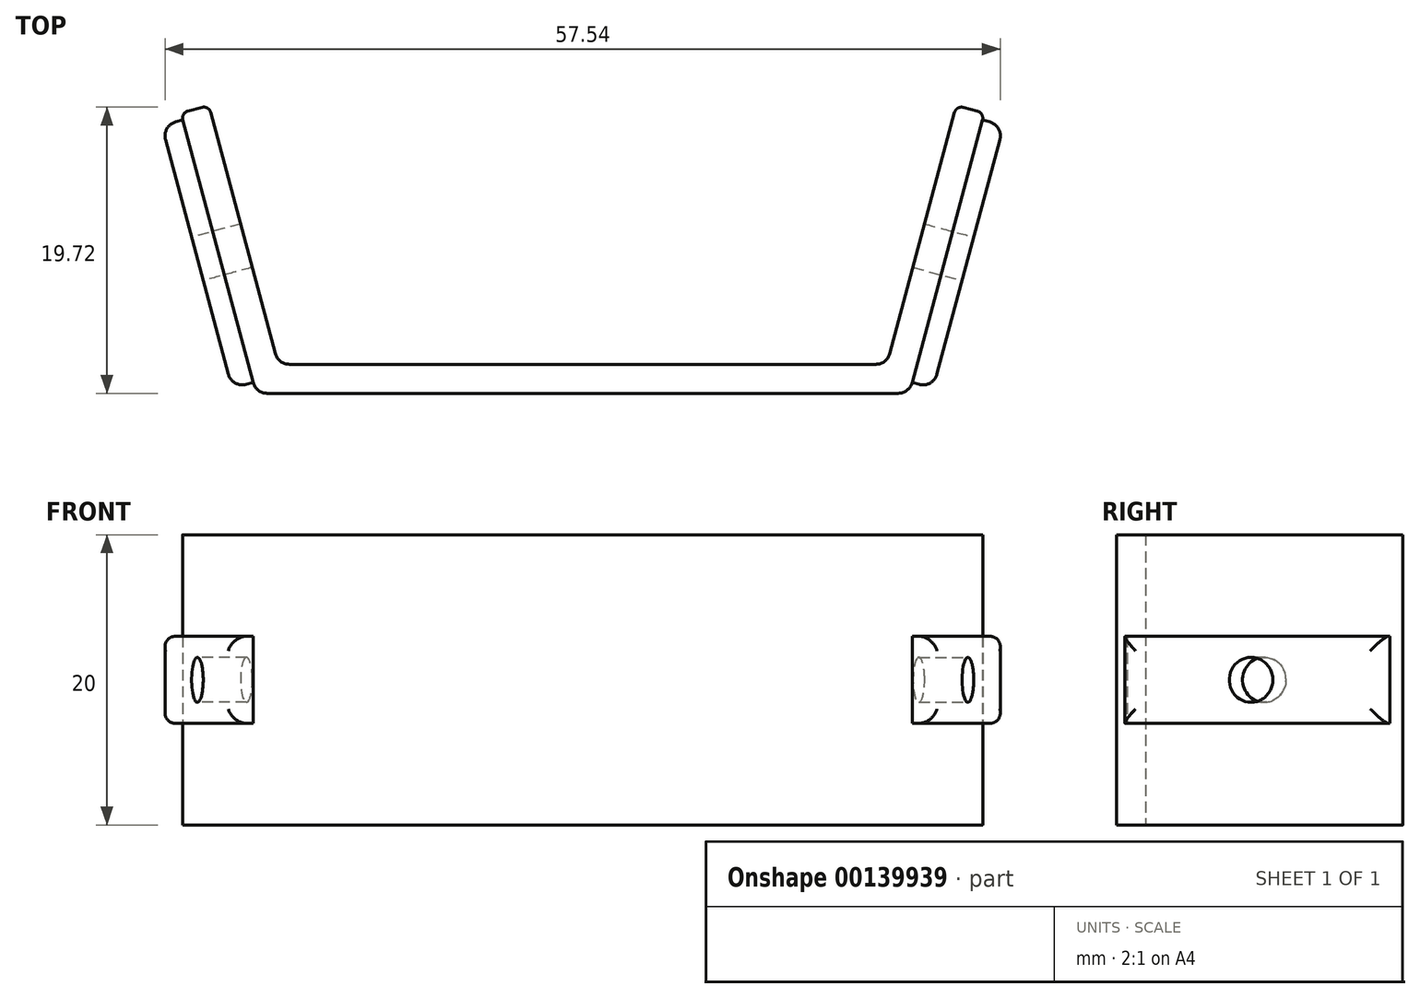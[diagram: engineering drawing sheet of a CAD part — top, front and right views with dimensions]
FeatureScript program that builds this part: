
annotation { "Feature Type Name" : "Feature", "Feature Type Description" : "" }
export const myFeature = defineFeature(function(context is Context, id is Id, definition is map)
    precondition{}
    {
        {
            var Q0;
            Q0=qCreatedBy(makeId("Top.planeOp"),FACE);
            var sketch = newSketch(context, id + "F0", { "sketchPlane" : qUnion([Q0])});
            skLineSegment(sketch, "E0", {"start": v(0.77, 0) * mm, "end": v(44.23, 0) * mm});
            skLineSegment(sketch, "E1", {"start": v(45.2, 0.74) * mm, "end": v(50.05, 18.84) * mm});
            skLineSegment(sketch, "E2", {"start": v(49.7, 19.45) * mm, "end": v(48.73, 19.7) * mm});
            skLineSegment(sketch, "E3", {"start": v(48.12, 19.35) * mm, "end": v(43.66, 2.74) * mm});
            skLineSegment(sketch, "E4", {"start": v(42.7, 2) * mm, "end": v(2.3, 2) * mm});
            skLineSegment(sketch, "E5", {"start": v(1.34, 2.74) * mm, "end": v(-3.12, 19.35) * mm});
            skLineSegment(sketch, "E6", {"start": v(-3.73, 19.7) * mm, "end": v(-4.7, 19.45) * mm});
            skLineSegment(sketch, "E7", {"start": v(-5.05, 18.84) * mm, "end": v(-0.2, 0.74) * mm});
            skPoint(sketch, "E8.visualSharp", {"position": v(-3.24, 19.84) * mm});
            skArc(sketch, "E8.filletArc", {"start": v(-3.12, 19.35) * mm, "mid": v(-3.35, 19.66) * mm, "end": v(-3.73, 19.7) * mm});
            skPoint(sketch, "E9.visualSharp", {"position": v(-5.18, 19.32) * mm});
            skArc(sketch, "E9.filletArc", {"start": v(-4.7, 19.45) * mm, "mid": v(-5, 19.21) * mm, "end": v(-5.05, 18.84) * mm});
            skPoint(sketch, "E10.visualSharp", {"position": v(0, 0) * mm});
            skArc(sketch, "E10.filletArc", {"start": v(-0.2, 0.74) * mm, "mid": v(0.16, 0.2) * mm, "end": v(0.77, 0) * mm});
            skPoint(sketch, "E11.visualSharp", {"position": v(1.53, 2) * mm});
            skArc(sketch, "E11.filletArc", {"start": v(1.34, 2.74) * mm, "mid": v(1.7, 2.2) * mm, "end": v(2.3, 2) * mm});
            skPoint(sketch, "E12.visualSharp", {"position": v(45, 0) * mm});
            skArc(sketch, "E12.filletArc", {"start": v(44.23, 0) * mm, "mid": v(44.84, 0.2) * mm, "end": v(45.2, 0.74) * mm});
            skPoint(sketch, "E13.visualSharp", {"position": v(43.47, 2) * mm});
            skArc(sketch, "E13.filletArc", {"start": v(42.7, 2) * mm, "mid": v(43.3, 2.2) * mm, "end": v(43.66, 2.74) * mm});
            skPoint(sketch, "E14.visualSharp", {"position": v(48.24, 19.84) * mm});
            skArc(sketch, "E14.filletArc", {"start": v(48.73, 19.7) * mm, "mid": v(48.35, 19.66) * mm, "end": v(48.12, 19.35) * mm});
            skPoint(sketch, "E15.visualSharp", {"position": v(50.18, 19.32) * mm});
            skArc(sketch, "E15.filletArc", {"start": v(50.05, 18.84) * mm, "mid": v(50, 19.21) * mm, "end": v(49.7, 19.45) * mm});
            skSolve(sketch);
        }
        {
            var Q0;
            Q0 = qSketchRegion(id + "F0", true);
            extrude(context, id + "F1", {"entities" : qUnion([Q0]), "depth" : 20 * mm});
        }
        {
            var Q0;
            Q0=makeQuery(id+"F1.opExtrude","SWEPT_FACE",FACE,{"disambiguationData":[OSD([sQuery(id+"F0.wireOp",EDGE,"E1")])]});
            var sketch = newSketch(context, id + "F2", { "sketchPlane" : qUnion([Q0])});
            skLineSegment(sketch, "E16.bottom", {"start": v(31.15, 7) * mm, "end": v(12.41, 7) * mm});
            skLineSegment(sketch, "E16.top", {"start": v(31.15, 13) * mm, "end": v(12.41, 13) * mm});
            skLineSegment(sketch, "E16.left", {"start": v(31.15, 7) * mm, "end": v(31.15, 13) * mm});
            skLineSegment(sketch, "E16.right", {"start": v(12.41, 7) * mm, "end": v(12.41, 13) * mm});
            skSolve(sketch);
        }
        {
            var Q0;
            Q0 = qSketchRegion(id + "F2", true);
            extrude(context, id + "F3", {"entities" : qUnion([Q0]), "operationType" : NewBodyOperationType.ADD, "depth" : 1.5 * mm});
        }
        {
            var Q0;
            Q0=makeQuery(id+"F1.opExtrude","SWEPT_FACE",FACE,{"disambiguationData":[OSD([sQuery(id+"F0.wireOp",EDGE,"E7")])]});
            var sketch = newSketch(context, id + "F4", { "sketchPlane" : qUnion([Q0])});
            skLineSegment(sketch, "E17.bottom", {"start": v(-0.77, 7) * mm, "end": v(-19.5, 7) * mm});
            skLineSegment(sketch, "E17.top", {"start": v(-0.77, 13) * mm, "end": v(-19.5, 13) * mm});
            skLineSegment(sketch, "E17.left", {"start": v(-0.77, 7) * mm, "end": v(-0.77, 13) * mm});
            skLineSegment(sketch, "E17.right", {"start": v(-19.5, 7) * mm, "end": v(-19.5, 13) * mm});
            skSolve(sketch);
        }
        {
            var Q0;
            Q0 = qSketchRegion(id + "F4", true);
            extrude(context, id + "F5", {"entities" : qUnion([Q0]), "operationType" : NewBodyOperationType.ADD, "depth" : 1.5 * mm});
        }
        {
            var Q0;
            Q0=makeQuery(id+"F1.opExtrude","SWEPT_FACE",FACE,{"disambiguationData":[OSD([sQuery(id+"F0.wireOp",EDGE,"E7")])]});
            var sketch = newSketch(context, id + "F6", { "sketchPlane" : qUnion([Q0])});
            skCircle(sketch, "E18", {"center": v(-10, 10) * mm, "radius": 1.55 * mm});
            skSolve(sketch);
        }
        {
            var Q0;
            Q0 = qSketchRegion(id + "F6", true);
            extrude(context, id + "F7", {"entities" : qUnion([Q0]), "operationType" : NewBodyOperationType.REMOVE, "oppositeDirection" : true, "depth" : 25 * mm, "symmetric" : true});
        }
        {
            var Q0;
            Q0=makeQuery(id+"F1.opExtrude","SWEPT_FACE",FACE,{"disambiguationData":[OSD([sQuery(id+"F0.wireOp",EDGE,"E1")])]});
            var sketch = newSketch(context, id + "F8", { "sketchPlane" : qUnion([Q0])});
            skCircle(sketch, "E19", {"center": v(21.65, 10) * mm, "radius": 1.55 * mm});
            skSolve(sketch);
        }
        {
            var Q0;
            Q0 = qSketchRegion(id + "F8", true);
            extrude(context, id + "F9", {"entities" : qUnion([Q0]), "operationType" : NewBodyOperationType.REMOVE, "oppositeDirection" : true, "depth" : 25 * mm, "symmetric" : true});
        }
        {
            var Q0;
            Q0=makeQuery(id+"F5.opExtrude","CAP_EDGE",EDGE,{"disambiguationData":[OSD([sQuery(id+"F4.wireOp",EDGE,"E17.left")])],"isStart":false});
            var Q1;
            Q1=makeQuery(id+"F5.opExtrude","CAP_EDGE",EDGE,{"disambiguationData":[OSD([sQuery(id+"F4.wireOp",EDGE,"E17.bottom")])],"isStart":false});
            var Q2;
            Q2=makeQuery(id+"F5.opExtrude","CAP_EDGE",EDGE,{"disambiguationData":[OSD([sQuery(id+"F4.wireOp",EDGE,"E17.top")])],"isStart":false});
            var Q3;
            Q3=makeQuery(id+"F5.opExtrude","CAP_EDGE",EDGE,{"disambiguationData":[OSD([sQuery(id+"F4.wireOp",EDGE,"E17.right")])],"isStart":false});
            var Q4;
            Q4=makeQuery(id+"F3.opExtrude","CAP_EDGE",EDGE,{"disambiguationData":[OSD([sQuery(id+"F2.wireOp",EDGE,"E16.left")])],"isStart":false});
            var Q5;
            Q5=makeQuery(id+"F3.opExtrude","CAP_EDGE",EDGE,{"disambiguationData":[OSD([sQuery(id+"F2.wireOp",EDGE,"E16.bottom")])],"isStart":false});
            var Q6;
            Q6=makeQuery(id+"F3.opExtrude","CAP_EDGE",EDGE,{"disambiguationData":[OSD([sQuery(id+"F2.wireOp",EDGE,"E16.top")])],"isStart":false});
            var Q7;
            Q7=makeQuery(id+"F3.opExtrude","CAP_EDGE",EDGE,{"disambiguationData":[OSD([sQuery(id+"F2.wireOp",EDGE,"E16.right")])],"isStart":false});
            fillet(context, id + "F10", {"entities" : qUnion([Q0, Q1, Q2, Q3, Q4, Q5, Q6, Q7]), "radius" : 1 * mm, "tangentPropagation" : true, "allowEdgeOverflow" : false});
        }
    });
